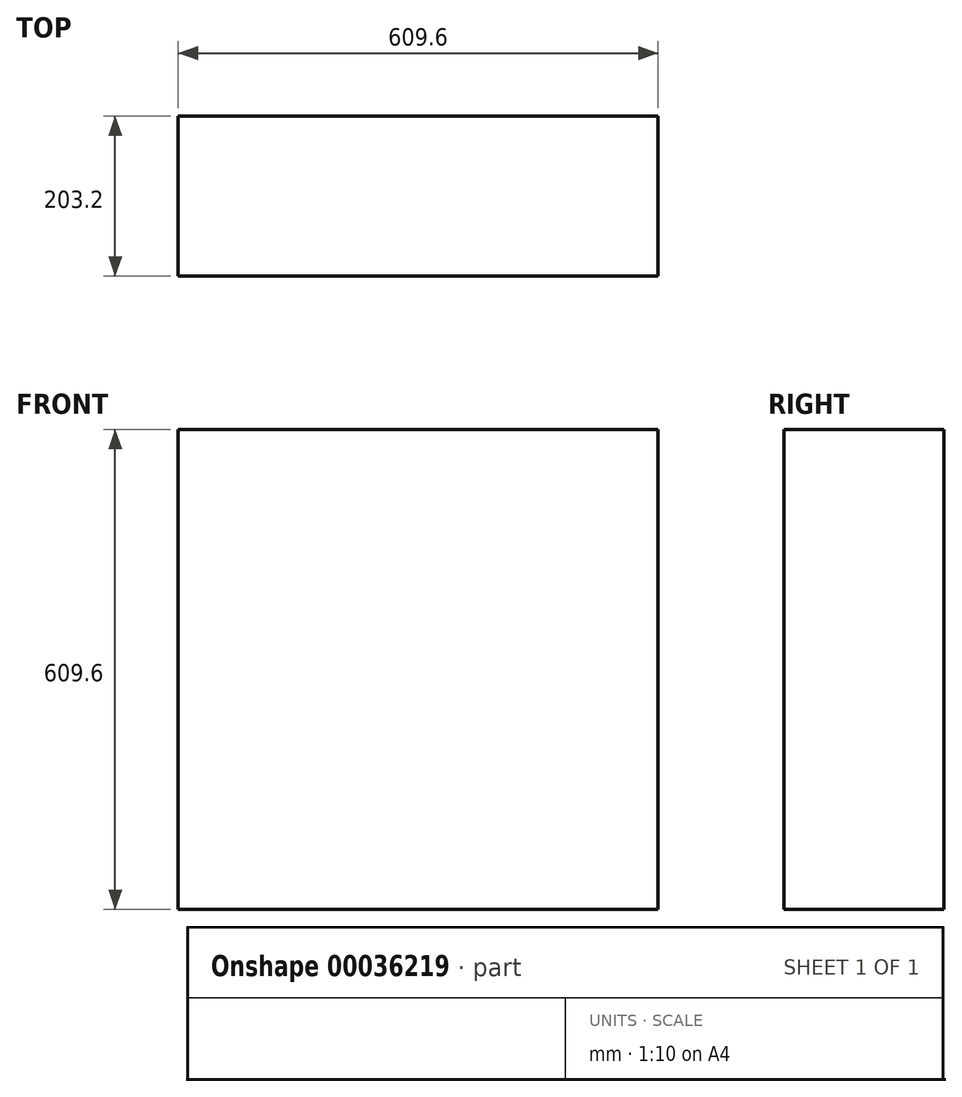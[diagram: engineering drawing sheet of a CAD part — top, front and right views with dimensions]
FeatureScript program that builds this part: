
annotation { "Feature Type Name" : "Feature", "Feature Type Description" : "" }
export const myFeature = defineFeature(function(context is Context, id is Id, definition is map)
    precondition{}
    {
        {
            var Q0;
            Q0=qCreatedBy(makeId("Front.planeOp"),FACE);
            var sketch = newSketch(context, id + "F0", { "sketchPlane" : qUnion([Q0])});
            skLineSegment(sketch, "E0.bottom", {"start": v(0, 0) * mm, "end": v(609.6, 0) * mm});
            skLineSegment(sketch, "E0.top", {"start": v(0, 609.6) * mm, "end": v(609.6, 609.6) * mm});
            skLineSegment(sketch, "E0.left", {"start": v(0, 0) * mm, "end": v(0, 609.6) * mm});
            skLineSegment(sketch, "E0.right", {"start": v(609.6, 0) * mm, "end": v(609.6, 609.6) * mm});
            skSolve(sketch);
        }
        {
            var Q0;
            Q0 = qSketchRegion(id + "F0", true);
            extrude(context, id + "F1", {"entities" : qUnion([Q0]), "depth" : 203.2 * mm});
        }
    });
